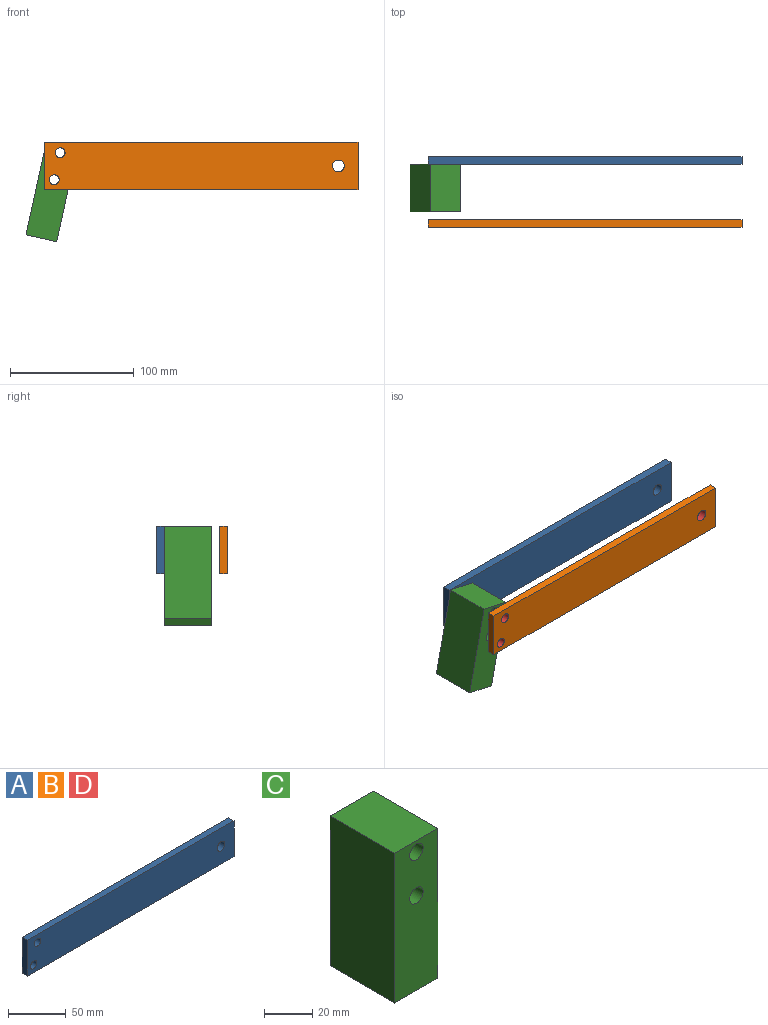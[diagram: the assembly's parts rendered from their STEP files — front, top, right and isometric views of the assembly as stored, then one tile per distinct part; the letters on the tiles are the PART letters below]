
ASSEMBLY  parts=4 mates=4
PART A: 9 faces, bbox 253.1x6.4x38.1 mm
  f0: plane 38.1x6.35mm, normal (1,0,0), area 241.9mm2, adj f1,f5,f7,f8
  f1: plane 253.06x6.35mm, normal (0,0,1), area 1606.9mm2, adj f0,f2,f7,f8
  f2: plane 38.1x6.35mm, normal (-1,0,0), area 241.9mm2, adj f1,f5,f7,f8
  f3: cylinder r=3.97mm len=7.94mm, axis (0,1,0), area 158.3mm2, adj f7,f8
  f4: cylinder r=4.76mm len=9.53mm, axis (0,1,0), area 190mm2, adj f7,f8
  f5: plane 253.06x6.35mm, normal (0,0,-1), area 1606.9mm2, adj f0,f2,f7,f8
  f6: cylinder r=3.97mm len=7.94mm, axis (0,1,0), area 158.3mm2, adj f7,f8
  f7: plane 253.06x38.1mm, normal (0,-1,0), area 9471.3mm2, adj f0,f1,f2,f3,f4,f5,f6
  f8: plane 253.06x38.1mm, normal (0,1,0), area 9471.3mm2, adj f0,f1,f2,f3,f4,f5,f6
PART B: same geometry as A
PART C: 8 faces, bbox 25.4x38.1x76.2 mm
  f0: plane 38.1x25.4mm, normal (0,0,1), area 967.7mm2, adj f1,f5,f6,f7
  f1: plane 76.2x38.1mm, normal (-1,0,0), area 2903.2mm2, adj f0,f2,f6,f7
  f2: plane 38.1x25.4mm, normal (0,0,-1), area 967.7mm2, adj f1,f5,f6,f7
  f3: cylinder r=3.97mm len=38.1mm, axis (0,1,0), area 950.1mm2, adj f6,f7
  f4: cylinder r=3.97mm len=38.1mm, axis (0,1,0), area 950.1mm2, adj f6,f7
  f5: plane 76.2x38.1mm, normal (1,0,0), area 2903.2mm2, adj f0,f2,f6,f7
  f6: plane 76.2x25.4mm, normal (0,-1,0), area 1836.5mm2, adj f0,f1,f2,f3,f4,f5
  f7: plane 76.2x25.4mm, normal (0,1,0), area 1836.5mm2, adj f0,f1,f2,f3,f4,f5
PART D: same geometry as A
PLACE A t=(0,50.8,0)mm
PLACE B at identity
PLACE C rot(axis=(0,1,0),12.4deg) t=(-224.48,44.45,10.6)mm
PLACE D at identity fixed
MATE cylindrical D.f6 <-> C.f3  axis (0,1,0) through (-224.48,0,10.6)mm
MATE revolute C.f3 <-> A.f6  axis (0,1,0) through (-224.48,44.45,10.6)mm
MATE cylindrical D.f3 <-> C.f4  axis (0,1,0) through (-229.25,0,-11.11)mm
MATE cylindrical C.f4 <-> A.f3  axis (0,1,0) through (-229.25,44.45,-11.11)mm
